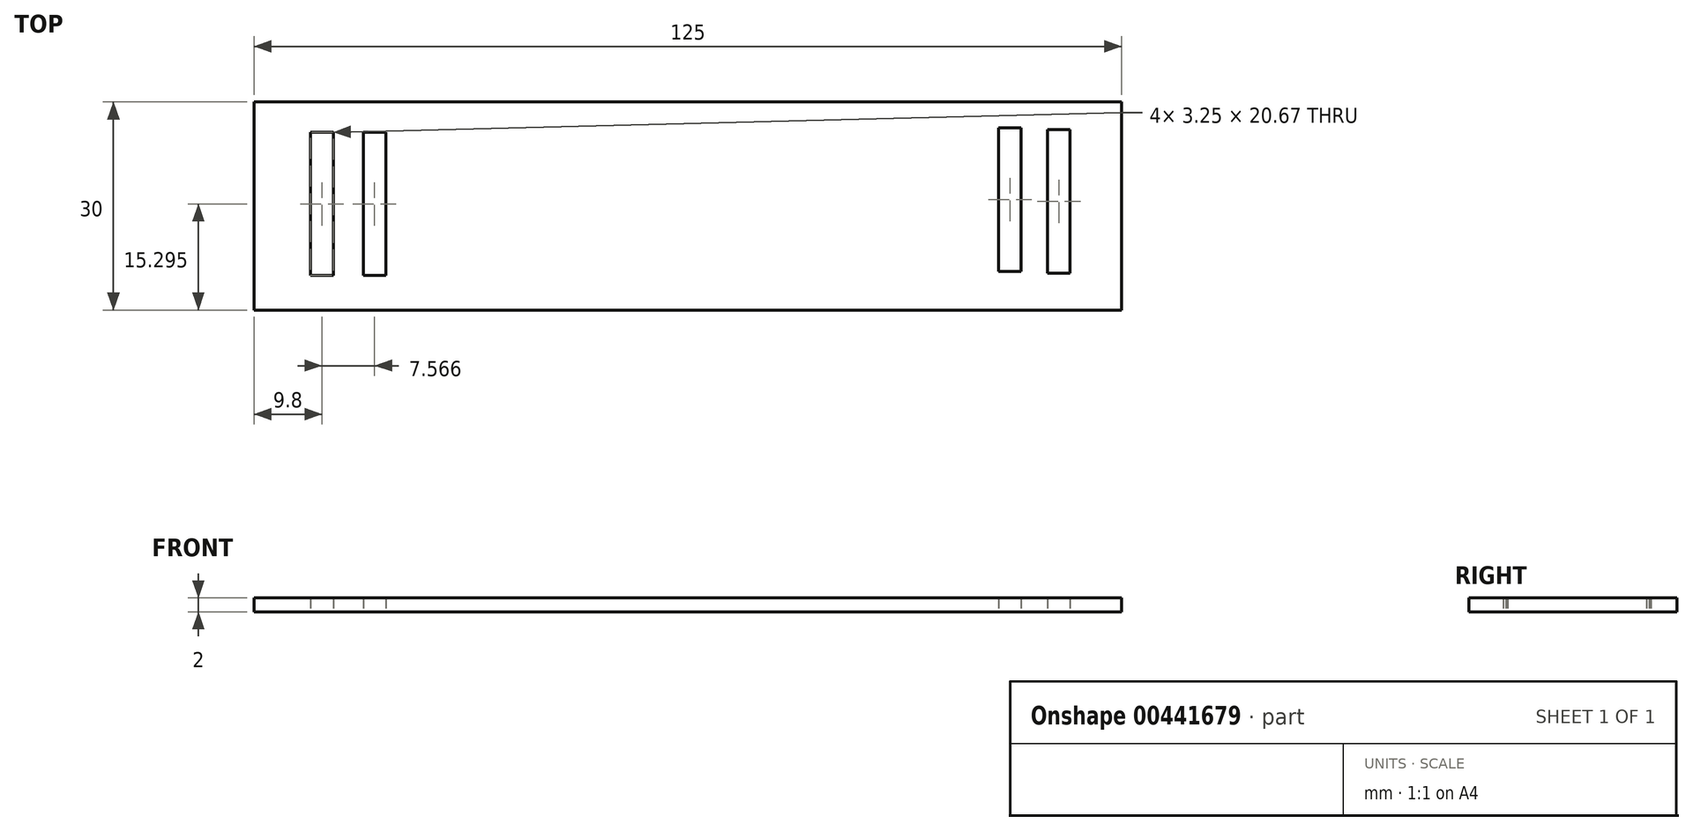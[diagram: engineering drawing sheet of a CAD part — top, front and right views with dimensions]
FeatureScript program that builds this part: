
annotation { "Feature Type Name" : "Feature", "Feature Type Description" : "" }
export const myFeature = defineFeature(function(context is Context, id is Id, definition is map)
    precondition{}
    {
        {
            var Q0;
            Q0=qCreatedBy(makeId("Top.planeOp"),FACE);
            var sketch = newSketch(context, id + "F0", { "sketchPlane" : qUnion([Q0])});
            skLineSegment(sketch, "E0.bottom", {"start": v(-62.5, 15) * mm, "end": v(62.5, 15) * mm});
            skLineSegment(sketch, "E0.top", {"start": v(-62.5, -15) * mm, "end": v(62.5, -15) * mm});
            skLineSegment(sketch, "E0.left", {"start": v(-62.5, 15) * mm, "end": v(-62.5, -15) * mm});
            skLineSegment(sketch, "E0.right", {"start": v(62.5, 15) * mm, "end": v(62.5, -15) * mm});
            skLineSegment(sketch, "E1.bottom", {"start": v(-54.32, 10.63) * mm, "end": v(-51.08, 10.63) * mm});
            skLineSegment(sketch, "E1.top", {"start": v(-54.32, -10.04) * mm, "end": v(-51.08, -10.04) * mm});
            skLineSegment(sketch, "E1.left", {"start": v(-54.32, 10.63) * mm, "end": v(-54.32, -10.04) * mm});
            skLineSegment(sketch, "E1.right", {"start": v(-51.08, 10.63) * mm, "end": v(-51.08, -10.04) * mm});
            skLineSegment(sketch, "E2.bottom", {"start": v(51.83, 11) * mm, "end": v(55.08, 11) * mm});
            skLineSegment(sketch, "E2.top", {"start": v(51.83, -9.67) * mm, "end": v(55.08, -9.67) * mm});
            skLineSegment(sketch, "E2.left", {"start": v(51.83, 11) * mm, "end": v(51.83, -9.67) * mm});
            skLineSegment(sketch, "E2.right", {"start": v(55.08, 11) * mm, "end": v(55.08, -9.67) * mm});
            skLineSegment(sketch, "E3.bottom", {"start": v(44.8, 11.25) * mm, "end": v(48.04, 11.25) * mm});
            skLineSegment(sketch, "E3.top", {"start": v(44.8, -9.41) * mm, "end": v(48.04, -9.41) * mm});
            skLineSegment(sketch, "E3.left", {"start": v(44.8, 11.25) * mm, "end": v(44.8, -9.41) * mm});
            skLineSegment(sketch, "E3.right", {"start": v(48.04, 11.25) * mm, "end": v(48.04, -9.41) * mm});
            skLineSegment(sketch, "E4.bottom", {"start": v(-46.76, 10.63) * mm, "end": v(-43.51, 10.63) * mm});
            skLineSegment(sketch, "E4.top", {"start": v(-46.76, -10.04) * mm, "end": v(-43.51, -10.04) * mm});
            skLineSegment(sketch, "E4.left", {"start": v(-46.76, 10.63) * mm, "end": v(-46.76, -10.04) * mm});
            skLineSegment(sketch, "E4.right", {"start": v(-43.51, 10.63) * mm, "end": v(-43.51, -10.04) * mm});
            skSolve(sketch);
        }
        {
            var Q0;
            Q0=makeQuery(id+"F0.imprint","IMPRINT",FACE,{"disambiguationData":[TD([[makeQuery(id+"F0.imprint","IMPRINT",EDGE,{"derivedFrom":sQuery(id+"F0.wireOp",EDGE,"E0.bottom")}),-1.0]])]});
            extrude(context, id + "F1", {"entities" : qUnion([Q0]), "depth" : 2 * mm});
        }
    });
